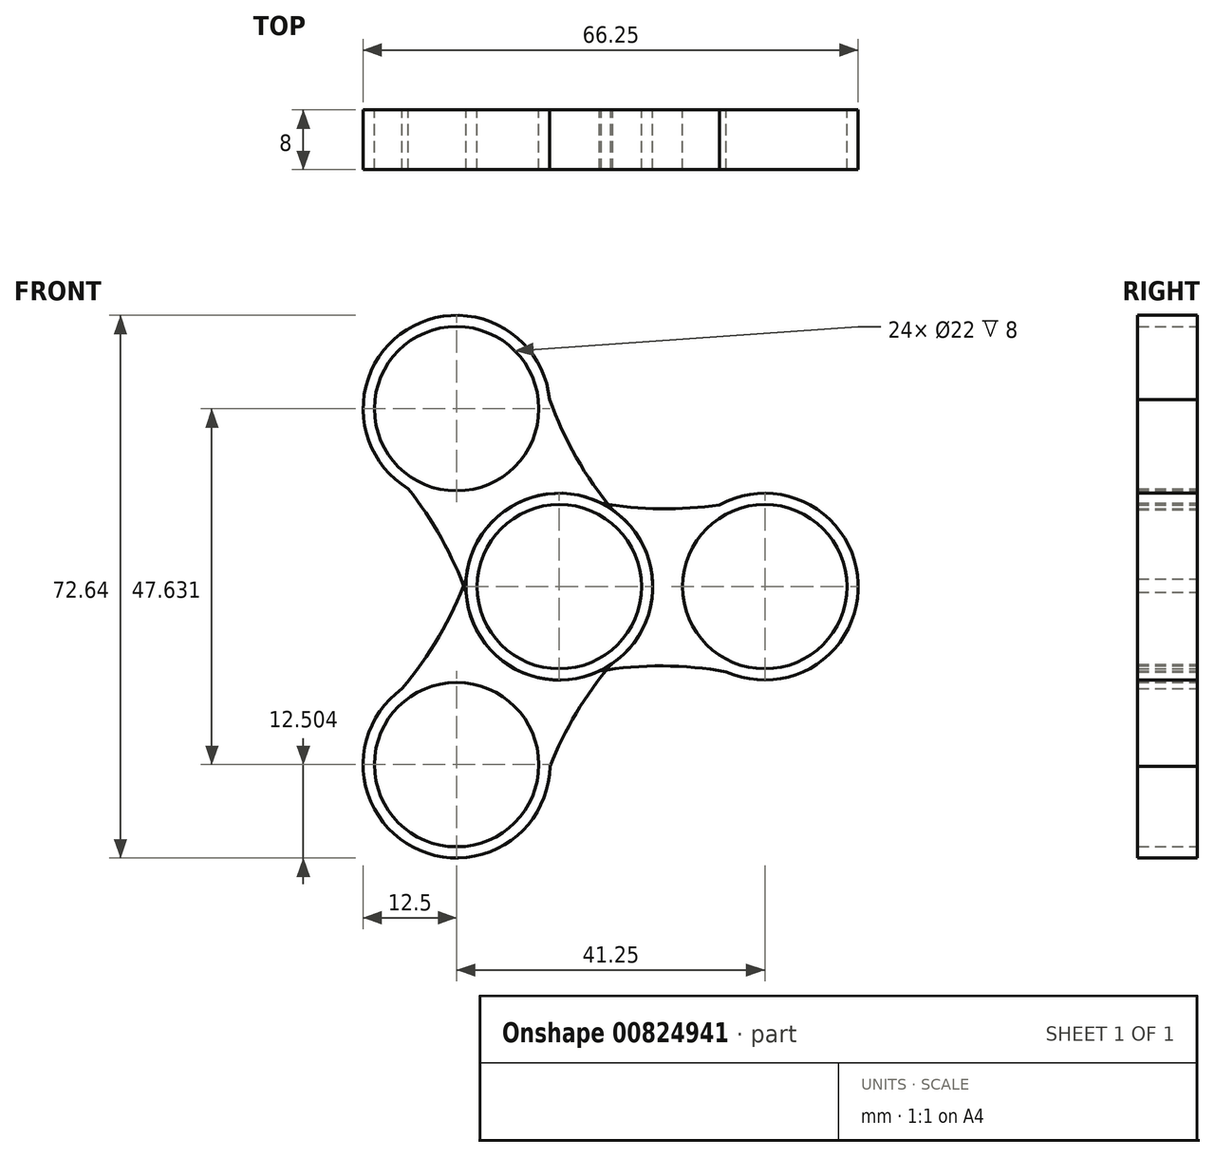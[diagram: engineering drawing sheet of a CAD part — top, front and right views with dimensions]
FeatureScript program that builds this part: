
annotation { "Feature Type Name" : "Feature", "Feature Type Description" : "" }
export const myFeature = defineFeature(function(context is Context, id is Id, definition is map)
    precondition{}
    {
        {
            var Q0;
            Q0=qCreatedBy(makeId("Front.planeOp"),FACE);
            var sketch = newSketch(context, id + "F0", { "sketchPlane" : qUnion([Q0])});
            skCircle(sketch, "E0", {"center": v(0, 0) * mm, "radius": 12.5 * mm});
            skCircle(sketch, "E1", {"center": v(0, 0) * mm, "radius": 11 * mm});
            skCircle(sketch, "E2", {"center": v(27.5, 0) * mm, "radius": 11 * mm});
            skCircle(sketch, "E3", {"center": v(27.5, 0) * mm, "radius": 12.5 * mm});
            skArc(sketch, "E4", {"start": v(0, 12.5) * mm, "mid": v(14.2, 10.42) * mm, "end": v(28.41, 12.47) * mm});
            skArc(sketch, "E5", {"start": v(27.17, -12.5) * mm, "mid": v(13.59, -10.62) * mm, "end": v(0, -12.5) * mm});
            skSolve(sketch);
        }
        {
            var Q0;
            Q0 = qSketchRegion(id + "F0", true);
            extrude(context, id + "F1", {"entities" : qUnion([Q0]), "depth" : 8 * mm, "offsetDistance" : 25 * mm});
        }
        {
            var Q0;
            Q0=qCreatedBy(makeId("Top.planeOp"),FACE);
            var sketch = newSketch(context, id + "F2", { "sketchPlane" : qUnion([Q0])});
            skLineSegment(sketch, "E6", {"start": v(0, 0) * mm, "end": v(0, -38.74) * mm, "construction": true});
            skSolve(sketch);
        }
        {
            var Q0;
            Q0=makeQuery(id+"F1.opExtrude","SWEPT_BODY",BODY,{"disambiguationData":[OSD([sQuery(id+"F0.wireOp",EDGE,"E0"),sQuery(id+"F0.wireOp",EDGE,"E1"),sQuery(id+"F0.wireOp",EDGE,"E2"),sQuery(id+"F0.wireOp",EDGE,"E3"),sQuery(id+"F0.wireOp",EDGE,"E4"),sQuery(id+"F0.wireOp",EDGE,"E5")])]});
            var Q1;
            Q1=sQuery(id+"F2.wireOp",EDGE,"E6");
            circularPattern(context, id + "F3", {"entities" : qUnion([Q0]), "axis" : qUnion([Q1]), "angle" : 360 * degree, "instanceCount" : 3, "equalSpace" : true});
        }
    });
